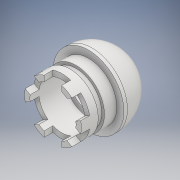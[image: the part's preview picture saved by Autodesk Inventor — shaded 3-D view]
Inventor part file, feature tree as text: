
AUTODESK INVENTOR PART (.ipt)
format: ipt  version: 2018 (Build 220112000, 112)  size: 208,384 bytes
history: native  units: mm
features: sketch x4, revolve x2, extrude x2, pattern_circular x1
ambient origin geometry x8: Origin, YZ Plane, XZ Plane, XY Plane, X Axis, Y Axis, Z Axis, Center Point
bodies: Solid1 (feature_tree)
feature tree (9):
  revolve  "Revolution1"  [1 undecoded]
  extrude  "Extrusion1"  TaperAngle=90.0deg  [1 undecoded]
  pattern_circular  "Circular Pattern1"  [2 undecoded]
  extrude  "Extrusion2"  Depth=10.0mm TaperAngle=0.0deg
  revolve  "Revolution2"  Angle=360.0deg
  sketch  "Sketch1"  dims[d0=3.0mm d1=2.0mm]
  sketch  "Sketch2"  dims[d3=20.0mm d6=90.0deg]
  sketch  "Sketch3"  dims[d7=10.0mm]
  sketch  "Sketch4"  dims[d8=15.0mm d9=20.0mm d10=10.0mm d11=0.0mm d12=60.0mm d13=360.0deg d15=20.0mm d16=15.5mm d17=0.0mm d18=1.5mm d19=3.5mm d20=90.0deg d21=7.0mm d22=4.0mm d23=20.0mm]
note: 4 required parameter values undecoded (feature->parameter linkage not recoverable at this tier; creation-order binding heuristic only, values carry confidence <= 0.55)